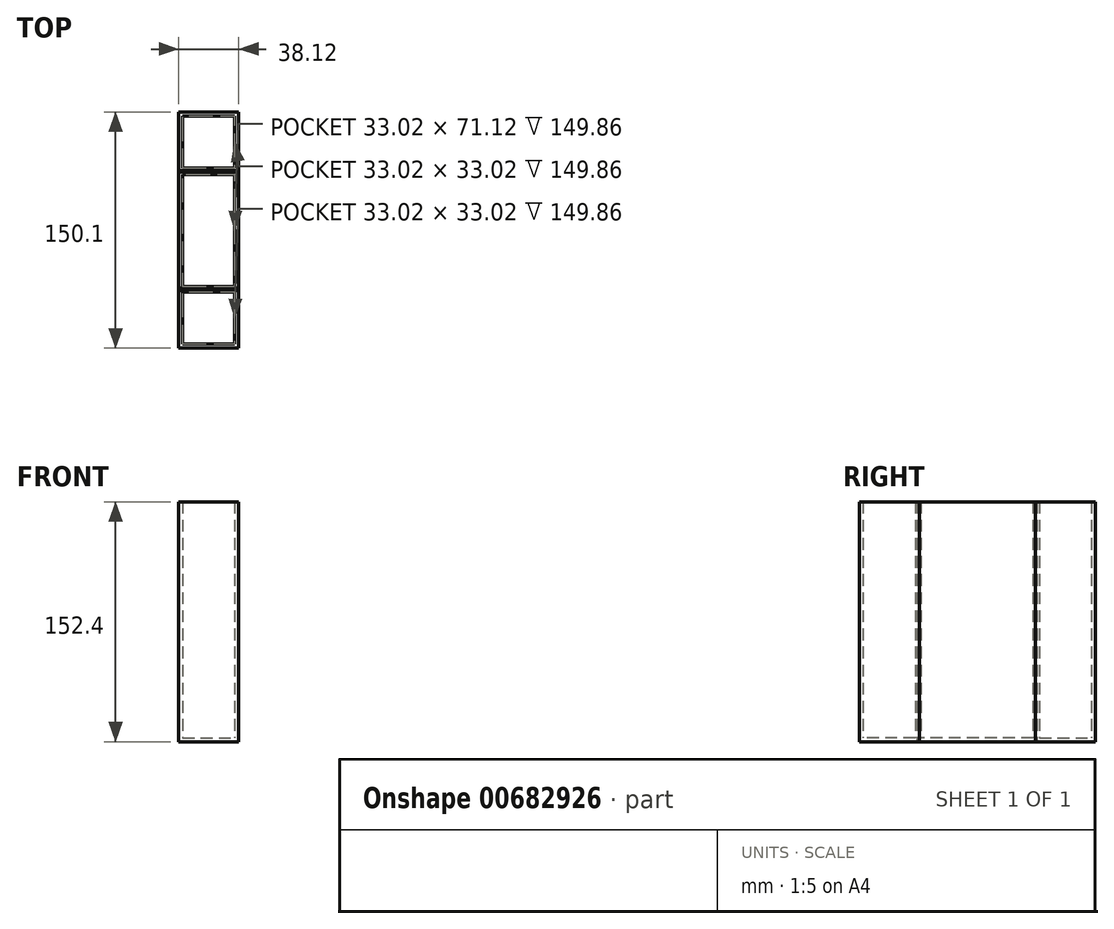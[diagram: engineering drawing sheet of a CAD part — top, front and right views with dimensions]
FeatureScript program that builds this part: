
annotation { "Feature Type Name" : "Feature", "Feature Type Description" : "" }
export const myFeature = defineFeature(function(context is Context, id is Id, definition is map)
    precondition{}
    {
        {
            var Q0;
            Q0=qCreatedBy(makeId("Top.planeOp"),FACE);
            var sketch = newSketch(context, id + "F0", { "sketchPlane" : qUnion([Q0])});
            skLineSegment(sketch, "E0.bottom", {"start": v(-18.2, 77.35) * mm, "end": v(19.9, 77.35) * mm});
            skLineSegment(sketch, "E0.top", {"start": v(-18.2, -75.05) * mm, "end": v(19.9, -75.05) * mm});
            skLineSegment(sketch, "E0.left", {"start": v(-18.2, 77.35) * mm, "end": v(-18.2, -75.05) * mm});
            skLineSegment(sketch, "E0.right", {"start": v(19.9, 77.35) * mm, "end": v(19.9, -75.05) * mm});
            skLineSegment(sketch, "E1.bottom", {"start": v(-18.08, 77.35) * mm, "end": v(20.02, 77.35) * mm});
            skLineSegment(sketch, "E1.top", {"start": v(-18.08, 39.25) * mm, "end": v(20.02, 39.25) * mm});
            skLineSegment(sketch, "E1.left", {"start": v(-18.08, 77.35) * mm, "end": v(-18.08, 39.25) * mm});
            skLineSegment(sketch, "E1.right", {"start": v(20.02, 77.35) * mm, "end": v(20.02, 39.25) * mm});
            skLineSegment(sketch, "E2.bottom", {"start": v(-18.2, -36.95) * mm, "end": v(19.9, -36.95) * mm});
            skLineSegment(sketch, "E2.left", {"start": v(-18.2, -36.95) * mm, "end": v(-18.2, -75.05) * mm});
            skLineSegment(sketch, "E2.right", {"start": v(19.9, -36.95) * mm, "end": v(19.9, -75.05) * mm});
            skSolve(sketch);
        }
        {
            var Q0;
            Q0=makeQuery(id+"F0.imprint","IMPRINT",FACE,{"disambiguationData":[TD([[makeQuery(id+"F0.imprint","IMPRINT",EDGE,{"derivedFrom":sQuery(id+"F0.wireOp",EDGE,"E2.bottom")}),-1.0]])]});
            extrude(context, id + "F1", {"entities" : qUnion([Q0]), "depth" : 152.4 * mm, "offsetDistance" : 25.4 * mm});
        }
        {
            var Q0;
            Q0=makeQuery(id+"F1.opExtrude","CAP_FACE",FACE,{"disambiguationData":[OSD([sQuery(id+"F0.wireOp",EDGE,"E2.bottom"),sQuery(id+"F0.wireOp",EDGE,"E0.top"),sQuery(id+"F0.wireOp",EDGE,"E2.left"),sQuery(id+"F0.wireOp",EDGE,"E2.right")])],"isStart":false});
            shell(context, id + "F2", {"entities" : qUnion([Q0]), "thickness" : 2.54 * mm});
        }
        {
            var Q0;
            Q0=makeQuery(id+"F1.opExtrude","SWEPT_BODY",BODY,{"disambiguationData":[OSD([sQuery(id+"F0.wireOp",EDGE,"E2.bottom"),sQuery(id+"F0.wireOp",EDGE,"E0.top"),sQuery(id+"F0.wireOp",EDGE,"E2.left"),sQuery(id+"F0.wireOp",EDGE,"E2.right")])]});
            var Q1;
            Q1=qCreatedBy(makeId("Front.planeOp"),FACE);
            mirror(context, id + "F3", {"entities" : qUnion([Q0]), "mirrorPlane" : qUnion([Q1])});
        }
        {
            var Q0;
            Q0=qCreatedBy(makeId("Top.planeOp"),FACE);
            var sketch = newSketch(context, id + "F4", { "sketchPlane" : qUnion([Q0])});
            skLineSegment(sketch, "E3.bottom", {"start": v(-18.22, 37.9) * mm, "end": v(19.88, 37.9) * mm});
            skLineSegment(sketch, "E3.top", {"start": v(-18.22, -38.3) * mm, "end": v(19.88, -38.3) * mm});
            skLineSegment(sketch, "E3.left", {"start": v(-18.22, 37.9) * mm, "end": v(-18.22, -38.3) * mm});
            skLineSegment(sketch, "E3.right", {"start": v(19.88, 37.9) * mm, "end": v(19.88, -38.3) * mm});
            skSolve(sketch);
        }
        {
            var Q0;
            Q0=makeQuery(id+"F4.imprint","IMPRINT",FACE,{"disambiguationData":[TD([[makeQuery(id+"F4.imprint","IMPRINT",EDGE,{"derivedFrom":sQuery(id+"F4.wireOp",EDGE,"E3.bottom")}),-1.0]])]});
            extrude(context, id + "F5", {"entities" : qUnion([Q0]), "depth" : 152.4 * mm, "offsetDistance" : 25.4 * mm});
        }
        {
            var Q0;
            Q0=makeQuery(id+"F5.opExtrude","CAP_FACE",FACE,{"disambiguationData":[OSD([sQuery(id+"F4.wireOp",EDGE,"E3.bottom"),sQuery(id+"F4.wireOp",EDGE,"E3.top"),sQuery(id+"F4.wireOp",EDGE,"E3.left"),sQuery(id+"F4.wireOp",EDGE,"E3.right")])],"isStart":false});
            shell(context, id + "F6", {"entities" : qUnion([Q0]), "thickness" : 2.54 * mm});
        }
    });
